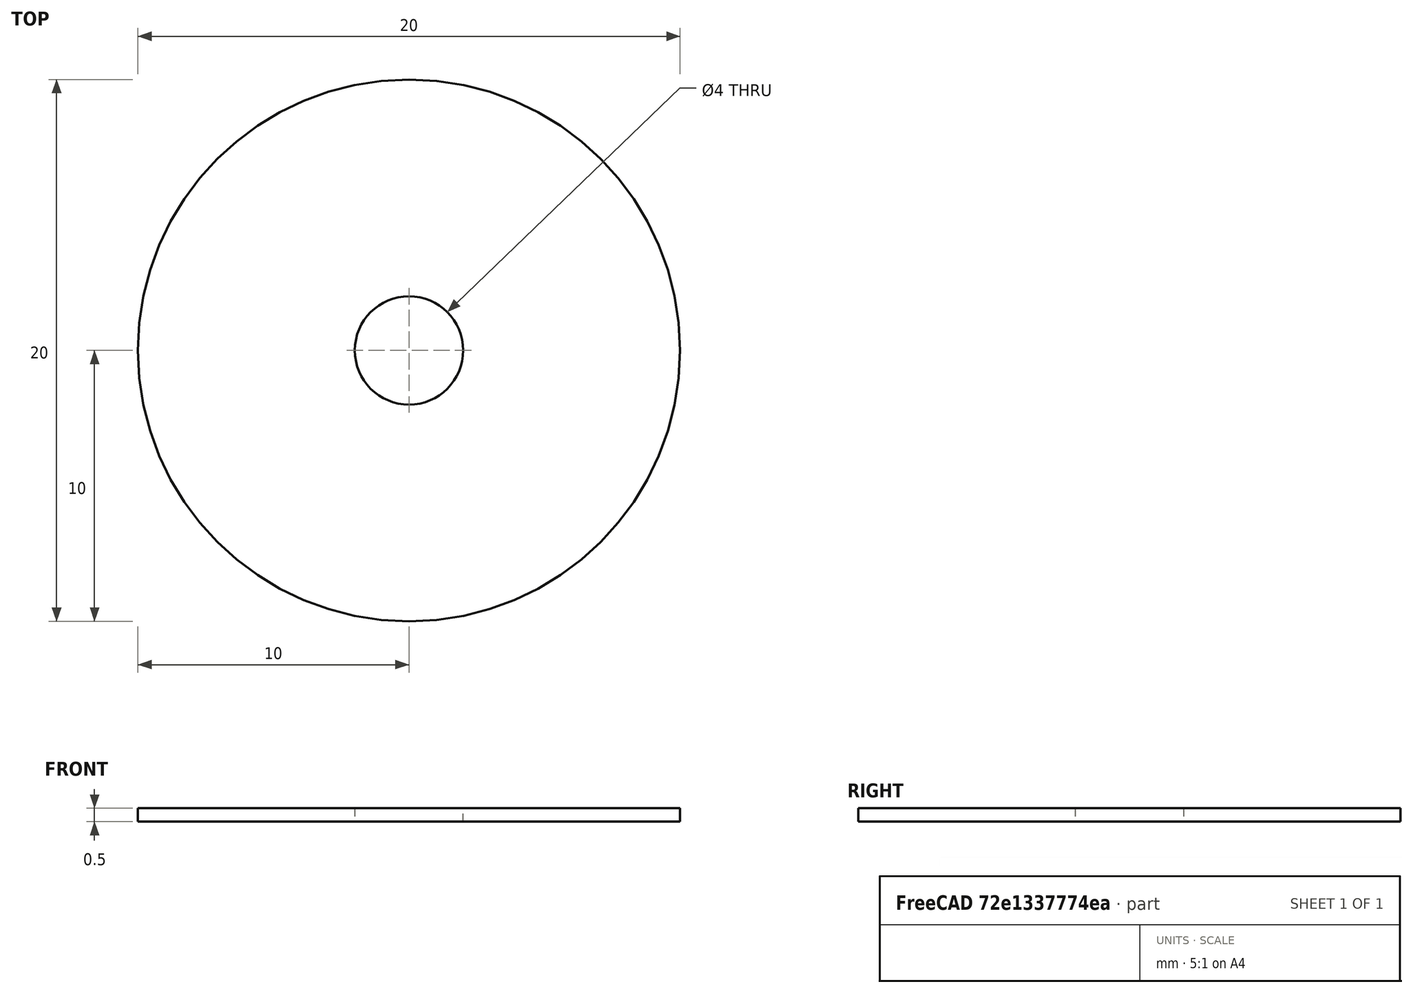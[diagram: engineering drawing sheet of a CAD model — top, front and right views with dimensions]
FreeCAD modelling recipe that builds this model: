
FCSTD DOCUMENT  (FreeCAD 0.20R27319 (Git))
Label: Disk
License: All rights reserved
LicenseURL: http://en.wikipedia.org/wiki/All_rights_reserved
objects: Sketcher::SketchObject×1, PartDesign::Pad×1, PartDesign::Body×1
note: 4 computed .brp shape members not serialized (recipe doc carries the construction recipe); baked Part::Feature solids carry a one-line shape summary decoded from their .brp

FEATURE [Sketcher::SketchObject] Sketch
  FullyConstrained = true
  MapMode = 5
  Support = -> [XY_Plane]
  sketch-geometry (2):
    g0: Circle CenterX=0 CenterY=0 CenterZ=0 NormalX=0 NormalY=0 NormalZ=1 AngleXU=0 Radius=2
    g1: Circle CenterX=0 CenterY=0 CenterZ=0 NormalX=0 NormalY=0 NormalZ=1 AngleXU=0 Radius=10
  constraints (4):
    c: Coincident(g0,g-1)
    c: Coincident(g1,g0)
    c: Diameter(g1) = 20
    c: Diameter(g0) = 4
FEATURE [PartDesign::Pad] Pad
  Direction = (0,0,1)
  Length = 0.5
  Length2 = 10
  Profile = -> Sketch
  ReferenceAxis = -> Sketch [N_Axis]
  Type = 0
FEATURE [PartDesign::Body] Body
  Group = -> [Sketch,Pad]
  Origin = -> Origin
  Tip = -> Pad
